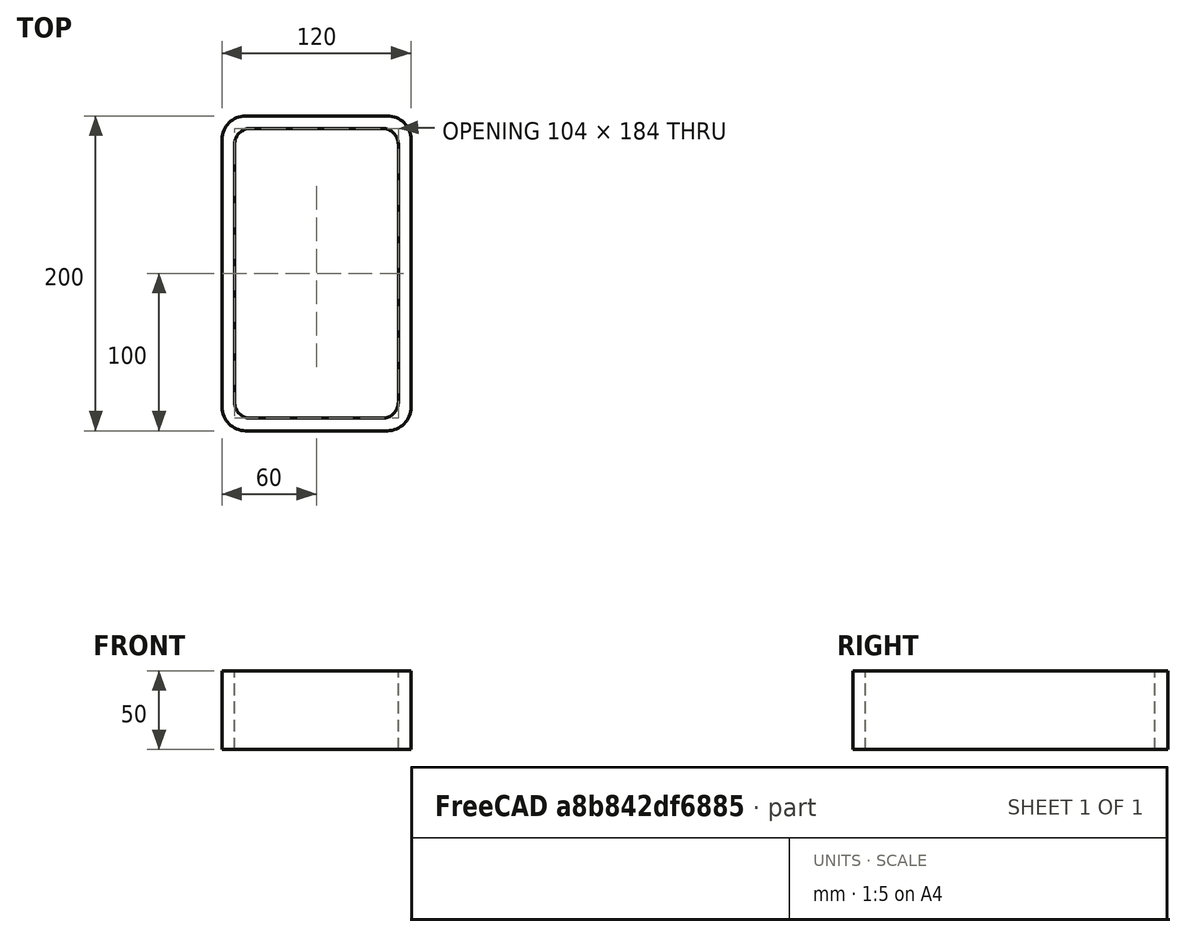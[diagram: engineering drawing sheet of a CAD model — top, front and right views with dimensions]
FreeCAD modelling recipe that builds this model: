
FCSTD DOCUMENT  (FreeCAD 0.15R4671 (Git))
Label: Rectangular hollow section 200x120x8 EN10219 S235JRH
License: All rights reserved
LicenseURL: http://en.wikipedia.org/wiki/All_rights_reserved
objects: Sketcher::SketchObject×1, Part::Extrusion×1
note: 2 computed .brp shape members not serialized (recipe doc carries the construction recipe); baked Part::Feature solids carry a one-line shape summary decoded from their .brp

FEATURE [Sketcher::SketchObject] Sketch
  sketch-geometry (16):
    g0: LineSegment StartX=-42 StartY=92 StartZ=0 EndX=42 EndY=92 EndZ=0
    g1: LineSegment StartX=52 StartY=82 StartZ=0 EndX=52 EndY=-82 EndZ=0
    g2: LineSegment StartX=42 StartY=-92 StartZ=0 EndX=-42 EndY=-92 EndZ=0
    g3: LineSegment StartX=-52 StartY=-82 StartZ=0 EndX=-52 EndY=82 EndZ=0
    g4: LineSegment StartX=-45 StartY=100 StartZ=0 EndX=45 EndY=100 EndZ=0
    g5: LineSegment StartX=60 StartY=85 StartZ=0 EndX=60 EndY=-85 EndZ=0
    g6: LineSegment StartX=45 StartY=-100 StartZ=0 EndX=-45 EndY=-100 EndZ=0
    g7: LineSegment StartX=-60 StartY=-85 StartZ=0 EndX=-60 EndY=85 EndZ=0
    g8: ArcOfCircle CenterX=-42 CenterY=82 CenterZ=0 NormalX=0 NormalY=0 NormalZ=1 Radius=10 StartAngle=1.5708 EndAngle=3.14159
    g9: ArcOfCircle CenterX=42 CenterY=82 CenterZ=0 NormalX=0 NormalY=0 NormalZ=1 Radius=10 StartAngle=0 EndAngle=1.5708
    g10: ArcOfCircle CenterX=42 CenterY=-82 CenterZ=0 NormalX=0 NormalY=0 NormalZ=1 Radius=10 StartAngle=4.71239 EndAngle=6.28319
    g11: ArcOfCircle CenterX=-42 CenterY=-82 CenterZ=0 NormalX=0 NormalY=0 NormalZ=1 Radius=10 StartAngle=3.14159 EndAngle=4.71239
    g12: ArcOfCircle CenterX=45 CenterY=85 CenterZ=0 NormalX=0 NormalY=0 NormalZ=1 Radius=15 StartAngle=0 EndAngle=1.5708
    g13: ArcOfCircle CenterX=45 CenterY=-85 CenterZ=0 NormalX=0 NormalY=0 NormalZ=1 Radius=15 StartAngle=4.71239 EndAngle=6.28319
    g14: ArcOfCircle CenterX=-45 CenterY=-85 CenterZ=0 NormalX=0 NormalY=0 NormalZ=1 Radius=15 StartAngle=3.14159 EndAngle=4.71239
    g15: ArcOfCircle CenterX=-45 CenterY=85 CenterZ=0 NormalX=0 NormalY=0 NormalZ=1 Radius=15 StartAngle=1.5708 EndAngle=3.14159
  constraints (36):
    c: Horizontal(g2)
    c: Vertical(g3)
    c: Horizontal(g6)
    c: Vertical(g7)
    c: Tangent(g3,g8) = 1.5708
    c: Tangent(g0,g8) = 1.5708
    c: Tangent(g0,g9) = 1.5708
    c: Tangent(g1,g9) = 1.5708
    c: Tangent(g1,g10) = 1.5708
    c: Tangent(g2,g10) = 1.5708
    c: Tangent(g2,g11) = 1.5708
    c: Tangent(g3,g11) = 1.5708
    c: Tangent(g4,g12) = 1.5708
    c: Tangent(g5,g12) = 1.5708
    c: Tangent(g5,g13) = 1.5708
    c: Tangent(g6,g13) = 1.5708
    c: Tangent(g6,g14) = 1.5708
    c: Tangent(g7,g14) = 1.5708
    c: Tangent(g7,g15) = 1.5708
    c: Tangent(g4,g15) = 1.5708
    c: Equal(g9,g8)
    c: Equal(g9,g11)
    c: Equal(g9,g10)
    c: Equal(g12,g15)
    c: Equal(g12,g14)
    c: Equal(g12,g13)
    c: Symmetric(g4,g6,g-1)
    c: Symmetric(g7,g5,g-2)
    c: DistanceY(g4,g6) = -200
    c: DistanceX(g7,g5) = 120
    c: Symmetric(g3,g1,g-2)
    c: Symmetric(g0,g2,g-1)
    c: DistanceY(g0,g4) = 8
    c: DistanceX(g5,g1) = -8
    c: Radius(g9) = 10
    c: Radius(g12) = 15
FEATURE [Part::Extrusion] Extrude  label="Rectangular hollow section 200x120x8 EN10219 S235JRH"
  Base = -> Sketch
  Dir = (0,0,50)
  Solid = true
